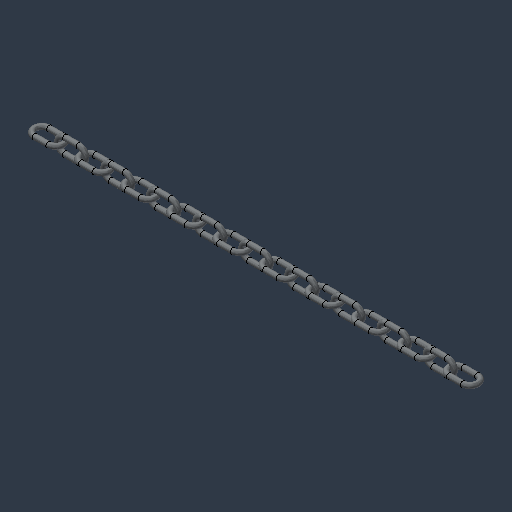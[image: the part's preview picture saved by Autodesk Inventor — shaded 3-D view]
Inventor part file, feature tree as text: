
AUTODESK INVENTOR PART (.ipt)
format: ipt  version: 2024.3 (Build 283343000, 343)  size: 760,320 bytes
history: native  units: mm (DEFAULTED — no unit token found)
features: other x17, sweep x2
ambient origin geometry x8: Origin, YZ Plane, XZ Plane, XY Plane, X Axis, Y Axis, Z Axis, Center Point
bodies: Solid1 (feature_tree), Solid2 (feature_tree), Solid3 (feature_tree), Solid4 (feature_tree), Solid5 (feature_tree), Solid6 (feature_tree), Solid7 (feature_tree), Solid8 (feature_tree), Solid9 (feature_tree), Solid10 (feature_tree), Solid11 (feature_tree), Solid12 (feature_tree), Solid13 (feature_tree), Solid14 (feature_tree), Solid15 (feature_tree), Solid16 (feature_tree), Solid17 (feature_tree), Solid18 (feature_tree), Solid19 (feature_tree)
feature tree (19):
  sweep  "Sweep1"
  sweep  "Sweep2"
  other  "LPattern1[1]"
  other  "LPattern1[2]"
  other  "LPattern1[3]"
  other  "LPattern1[4]"
  other  "LPattern1[5]"
  other  "LPattern1[6]"
  other  "LPattern1[7]"
  other  "LPattern1[8]"
  other  "LPattern1[9]"
  other  "LPattern1[10]"
  other  "LPattern1[11]"
  other  "LPattern1[12]"
  other  "LPattern1[13]"
  other  "LPattern1[14]"
  other  "LPattern1[15]"
  other  "LPattern1[16]"
  other  "LPattern3"
